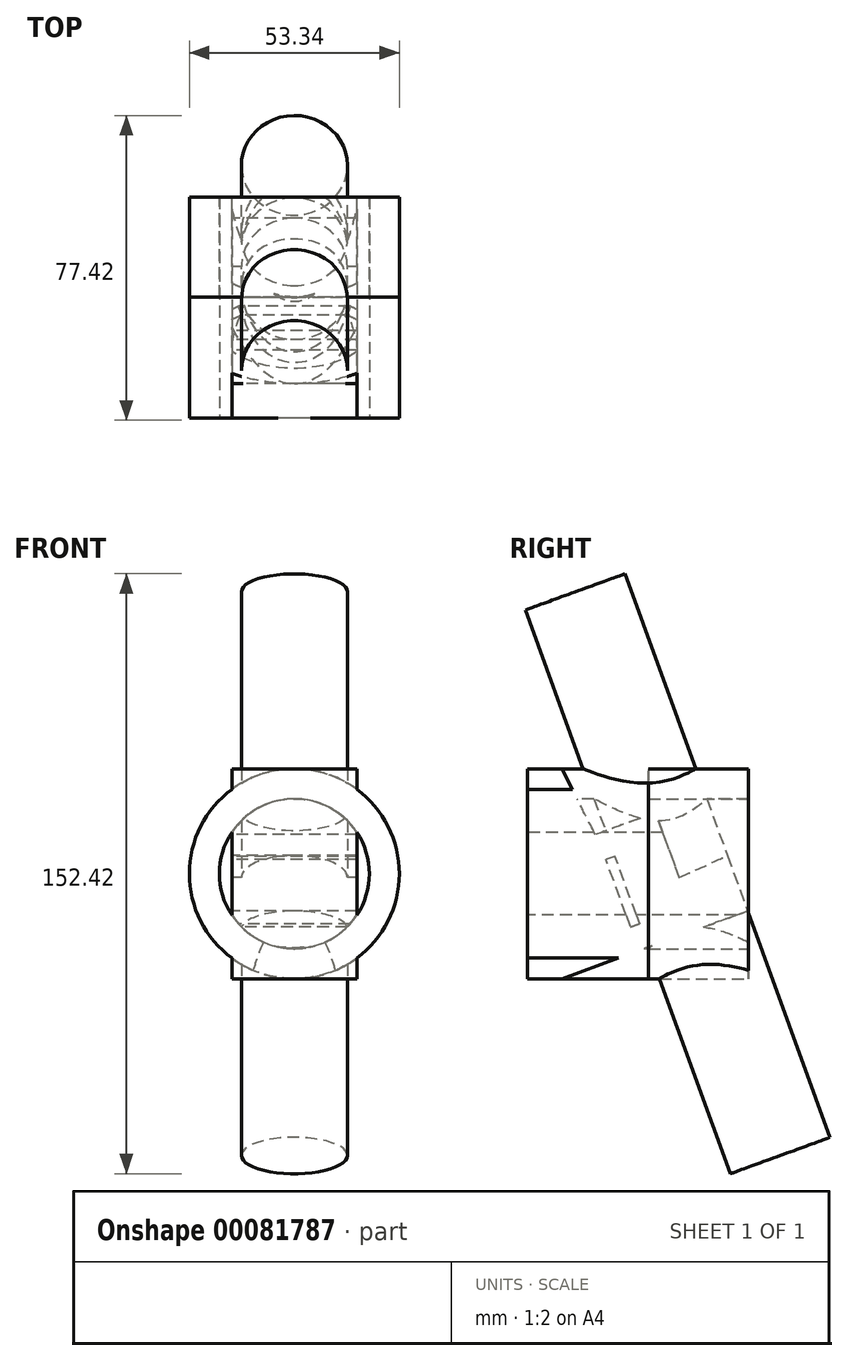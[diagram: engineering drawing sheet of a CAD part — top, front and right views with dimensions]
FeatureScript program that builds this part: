
annotation { "Feature Type Name" : "Feature", "Feature Type Description" : "" }
export const myFeature = defineFeature(function(context is Context, id is Id, definition is map)
    precondition{}
    {
        {
            var Q0;
            Q0=qCreatedBy(makeId("Top.planeOp"),FACE);
            var sketch = newSketch(context, id + "F0", { "sketchPlane" : qUnion([Q0])});
            skCircle(sketch, "E0", {"center": v(0, 0) * mm, "radius": 13.46 * mm});
            skSolve(sketch);
        }
        {
            var Q0;
            Q0=makeQuery(id+"F0.imprint","IMPRINT",FACE,{"disambiguationData":[TD([[makeQuery(id+"F0.imprint","IMPRINT",EDGE,{"derivedFrom":sQuery(id+"F0.wireOp",EDGE,"E0")}),1.0]])]});
            extrude(context, id + "F1", {"entities" : qUnion([Q0]), "endBound" : BoundingType.SYMMETRIC, "depth" : 152.4 * mm});
        }
        {
            var Q0;
            Q0=qCreatedBy(makeId("Top.planeOp"),FACE);
            var sketch = newSketch(context, id + "F2", { "sketchPlane" : qUnion([Q0])});
            skLineSegment(sketch, "E1", {"start": v(0, 0) * mm, "end": v(84.7, 0) * mm, "construction": true});
            skSolve(sketch);
        }
        {
            var Q0;
            Q0=makeQuery(id+"F1.opExtrude","SWEPT_BODY",BODY,{"disambiguationData":[OSD([sQuery(id+"F0.wireOp",EDGE,"E0")])]});
            var Q1;
            Q1=sQuery(id+"F2.wireOp",EDGE,"E1");
            transform(context, id + "F3", {"entities" : qUnion([Q0]), "transformType" : TransformType.ROTATION, "transformAxis" : qUnion([Q1]), "angle" : 20 * degree, "makeCopy" : false});
        }
        {
            var Q0;
            Q0=qCreatedBy(makeId("Front.planeOp"),FACE);
            cPlane(context, id + "F4", {"entities" : qUnion([Q0]), "cplaneType" : CPlaneType.OFFSET, "offset" : 38.1 * mm, "width" : 152.4 * mm, "height" : 152.4 * mm});
        }
        {
            var Q0;
            Q0=qCreatedBy(id+"F4.planeOp",FACE);
            var sketch = newSketch(context, id + "F5", { "sketchPlane" : qUnion([Q0])});
            skCircle(sketch, "E2", {"center": v(0, 0) * mm, "radius": 22.86 * mm});
            skCircle(sketch, "E3", {"center": v(0, 0) * mm, "radius": 19.05 * mm});
            skCircle(sketch, "E4", {"center": v(0, 0) * mm, "radius": 26.67 * mm});
            skSolve(sketch);
        }
        {
            var Q0;
            Q0=qCreatedBy(makeId("Right.planeOp"),FACE);
            var sketch = newSketch(context, id + "F6", { "sketchPlane" : qUnion([Q0])});
            skLineSegment(sketch, "E5.0", {"start": v(-38.1, -26.67) * mm, "end": v(-38.1, 26.67) * mm});
            skLineSegment(sketch, "E6", {"start": v(-38.1, -26.67) * mm, "end": v(-29.45, -26.67) * mm});
            skLineSegment(sketch, "E7", {"start": v(13.41, -76.2) * mm, "end": v(-38.71, 67) * mm});
            skLineSegment(sketch, "E8", {"start": v(-13.41, 76.2) * mm, "end": v(38.71, -67) * mm});
            skLineSegment(sketch, "E9", {"start": v(-29.45, -26.67) * mm, "end": v(17.78, -9.48) * mm});
            skLineSegment(sketch, "E10", {"start": v(17.78, -9.48) * mm, "end": v(7.01, 20.1) * mm});
            skLineSegment(sketch, "E11", {"start": v(7.01, 20.1) * mm, "end": v(-20.92, 9.93) * mm});
            skLineSegment(sketch, "E12", {"start": v(-20.92, 9.93) * mm, "end": v(-29.45, 26.67) * mm});
            skLineSegment(sketch, "E13", {"start": v(-29.45, 26.67) * mm, "end": v(-38.1, 26.67) * mm});
            skLineSegment(sketch, "E14", {"start": v(-15.94, 4.44) * mm, "end": v(-9.7, -12.7) * mm});
            skLineSegment(sketch, "E15", {"start": v(-9.7, -12.7) * mm, "end": v(-12, -13.54) * mm});
            skLineSegment(sketch, "E16", {"start": v(-12, -13.54) * mm, "end": v(-18.24, 3.6) * mm});
            skLineSegment(sketch, "E17", {"start": v(-15.94, 4.44) * mm, "end": v(-18.24, 3.6) * mm});
            skLineSegment(sketch, "E18", {"start": v(-5.64, 15.5) * mm, "end": v(5.13, -14.09) * mm});
            skFitSpline(sketch, "E19", {"points": [v(-38.1, 0) * mm, v(-22.77, -6.98) * mm, v(12.65, 4.6) * mm], "startDerivative": vector(33.9, -24.73) * mm, "endDerivative": vector(65.54, 30.35) * mm});
            skSolve(sketch);
        }
        {
            var Q0;
            Q0=sQuery(id+"F6.wireOp",EDGE,"E18");
            var Q1;
            Q1=qCreatedBy(id+"F4.planeOp",FACE);
            cPlane(context, id + "F7", {"entities" : qUnion([Q0, Q1]), "cplaneType" : CPlaneType.LINE_ANGLE, "offset" : 152.4 * mm, "angle" : 0 * degree, "width" : 152.4 * mm, "height" : 152.4 * mm});
        }
        {
            var Q0;
            Q0=makeQuery(id+"F5.imprint","IMPRINT",FACE,{"disambiguationData":[TD([[makeQuery(id+"F5.imprint","IMPRINT",EDGE,{"derivedFrom":sQuery(id+"F5.wireOp",EDGE,"E2")}),-1.0]])]});
            var Q1;
            Q1=makeQuery(id+"F5.imprint","IMPRINT",FACE,{"disambiguationData":[TD([[makeQuery(id+"F5.imprint","IMPRINT",EDGE,{"derivedFrom":sQuery(id+"F5.wireOp",EDGE,"E2")}),1.0]])]});
            extrude(context, id + "F8", {"entities" : qUnion([Q0, Q1]), "oppositeDirection" : true, "depth" : 56.07 * mm});
        }
        {
            var Q0;
            {var subQ0=sQuery(id+"F6.wireOp",EDGE,"E12");Q0=makeQuery(id+"F6.imprint","IMPRINT",FACE,{"disambiguationData":[TD([[makeQuery(id+"F6.imprint","IMPRINT",EDGE,{"derivedFrom":subQ0}),1.0]])]});}
            var Q1;
            {var subQ0=sQuery(id+"F6.wireOp",EDGE,"E18");var subQ1=sQuery(id+"F6.wireOp",EDGE,"E11");var subQ2=makeQuery(id+"F6.imprint","INTERSECT",VERTEX,{"derivedFrom":[subQ1,subQ0]});Q1=makeQuery(id+"F6.imprint","IMPRINT",FACE,{"disambiguationData":[TD([[makeQuery(id+"F6.imprint","IMPRINT",EDGE,{"disambiguationData":[TD([[subQ2,-1.0]])],"derivedFrom":subQ1}),1.0]])]});}
            var Q2;
            {var subQ0=sQuery(id+"F6.wireOp",EDGE,"E11");var subQ1=sQuery(id+"F6.wireOp",EDGE,"E10");var subQ2=makeQuery(id+"F6.imprint","INTERSECT",VERTEX,{"derivedFrom":[subQ1,subQ0]});Q2=makeQuery(id+"F6.imprint","IMPRINT",FACE,{"disambiguationData":[TD([[makeQuery(id+"F6.imprint","IMPRINT",EDGE,{"disambiguationData":[TD([[subQ2,1.0]])],"derivedFrom":subQ1}),1.0]])]});}
            var Q3;
            {var subQ0=sQuery(id+"F6.wireOp",EDGE,"E10");var subQ1=sQuery(id+"F6.wireOp",EDGE,"E9");var subQ2=makeQuery(id+"F6.imprint","INTERSECT",VERTEX,{"derivedFrom":[subQ1,subQ0]});Q3=makeQuery(id+"F6.imprint","IMPRINT",FACE,{"disambiguationData":[TD([[makeQuery(id+"F6.imprint","IMPRINT",EDGE,{"disambiguationData":[TD([[subQ2,1.0]])],"derivedFrom":subQ1}),1.0]])]});}
            var Q4;
            {var subQ0=sQuery(id+"F6.wireOp",EDGE,"E18");var subQ1=sQuery(id+"F6.wireOp",EDGE,"E9");var subQ2=makeQuery(id+"F6.imprint","INTERSECT",VERTEX,{"derivedFrom":[subQ1,subQ0]});Q4=makeQuery(id+"F6.imprint","IMPRINT",FACE,{"disambiguationData":[TD([[makeQuery(id+"F6.imprint","IMPRINT",EDGE,{"disambiguationData":[TD([[subQ2,1.0]])],"derivedFrom":subQ1}),1.0]])]});}
            var Q5;
            {var subQ1=sQuery(id+"F6.wireOp",EDGE,"E6");Q5=makeQuery(id+"F6.imprint","IMPRINT",FACE,{"disambiguationData":[TD([[makeQuery(id+"F6.imprint","IMPRINT",EDGE,{"derivedFrom":subQ1}),1.0]])]});}
            extrude(context, id + "F9", {"entities" : qUnion([Q0, Q1, Q2, Q3, Q4, Q5]), "endBound" : BoundingType.SYMMETRIC, "depth" : 31.75 * mm});
        }
        {
            var Q0;
            Q0=makeQuery(id+"F8.opExtrude","CAP_FACE",FACE,{"disambiguationData":[OSD([sQuery(id+"F5.wireOp",EDGE,"E3"),sQuery(id+"F5.wireOp",EDGE,"E4")])],"isStart":false});
            var sketch = newSketch(context, id + "F10", { "sketchPlane" : qUnion([Q0])});
            skSolve(sketch);
        }
        {
            var Q0;
            Q0=makeQuery(id+"F8.opExtrude","CAP_FACE",FACE,{"disambiguationData":[OSD([sQuery(id+"F5.wireOp",EDGE,"E3"),sQuery(id+"F5.wireOp",EDGE,"E4")])],"isStart":false});
            var Q1;
            Q1=makeQuery(id+"F10.imprint","IMPRINT",FACE,{"disambiguationData":[TD([[makeQuery(id+"F10.imprint","IMPRINT",EDGE,{"derivedFrom":makeQuery(id+"F8.opExtrude","CAP_EDGE",EDGE,{"disambiguationData":[OSD([sQuery(id+"F5.wireOp",EDGE,"E3")])],"isStart":false})}),-1.0]])]});
            extrude(context, id + "F11", {"entities" : qUnion([Q0, Q1]), "oppositeDirection" : true, "depth" : 25.4 * mm});
        }
        {
            var Q0;
            Q0=makeQuery(id+"F5.imprint","IMPRINT",FACE,{"disambiguationData":[TD([[makeQuery(id+"F5.imprint","IMPRINT",EDGE,{"derivedFrom":sQuery(id+"F5.wireOp",EDGE,"E2")}),-1.0]])]});
            extrude(context, id + "F12", {"entities" : qUnion([Q0]), "operationType" : NewBodyOperationType.ADD, "oppositeDirection" : true, "depth" : 25.4 * mm});
        }
    });
